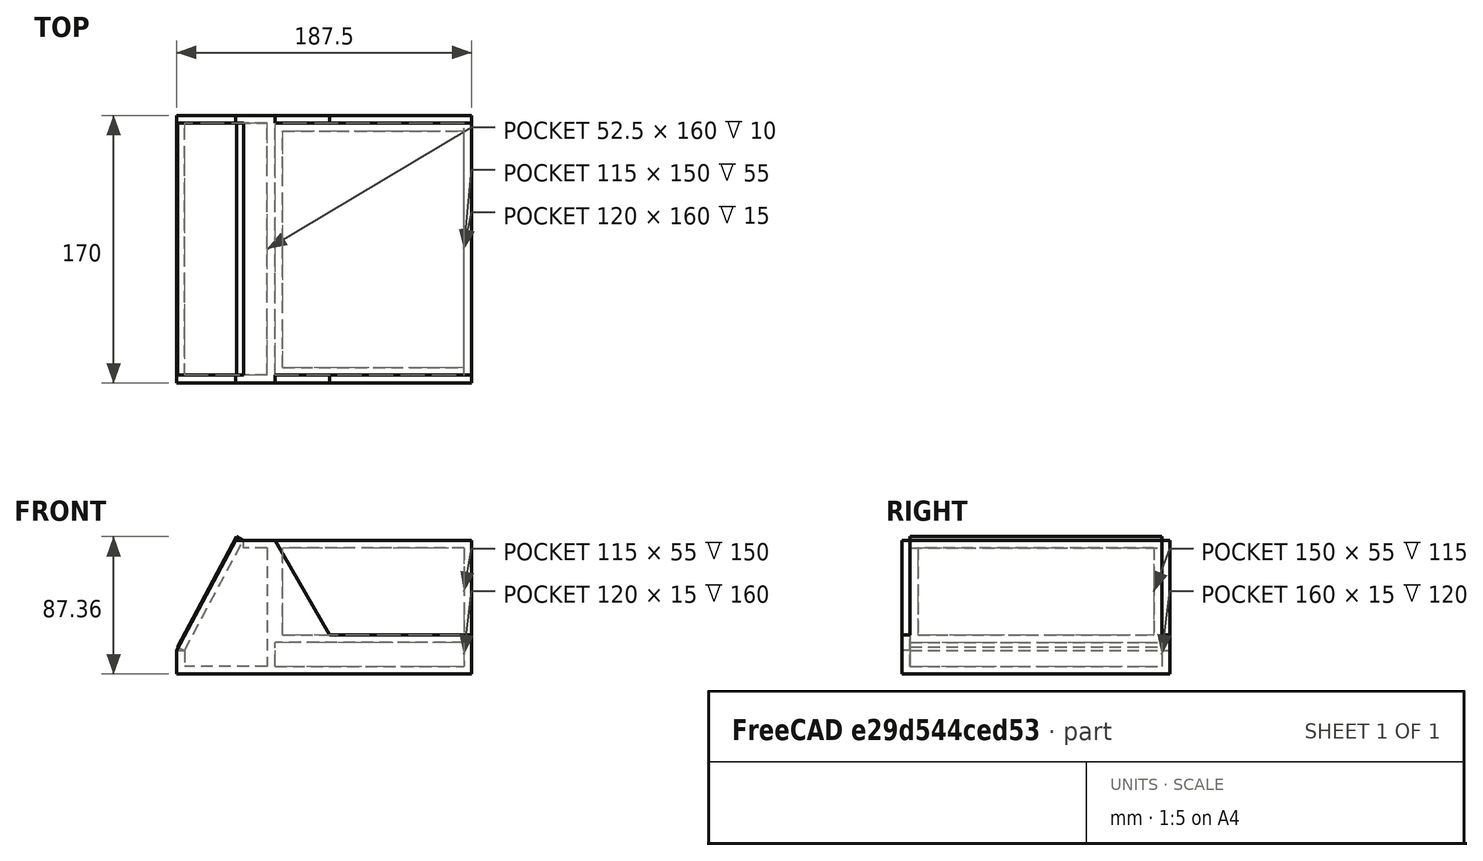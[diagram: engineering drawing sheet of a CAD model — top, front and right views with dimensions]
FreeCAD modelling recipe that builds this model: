
FCSTD DOCUMENT  (FreeCAD 0.17R13522 (Git))
Label: sheet model_no cut
License: All rights reserved
LicenseURL: http://en.wikipedia.org/wiki/All_rights_reserved
objects: Sketcher::SketchObject×12, PartDesign::Pad×12, PartDesign::Mirrored×2, PartDesign::Body×1
note: 39 computed .brp shape members not serialized (recipe doc carries the construction recipe); baked Part::Feature solids carry a one-line shape summary decoded from their .brp

FEATURE [Sketcher::SketchObject] Sketch
  MapMode = 5
  Support = -> [XY_Plane]
  sketch-geometry (4):
    g0: LineSegment StartX=-57.5 StartY=80 StartZ=0 EndX=120 EndY=80 EndZ=0
    g1: LineSegment StartX=120 StartY=80 StartZ=0 EndX=120 EndY=-80 EndZ=0
    g2: LineSegment StartX=120 StartY=-80 StartZ=0 EndX=-57.5 EndY=-80 EndZ=0
    g3: LineSegment StartX=-57.5 StartY=-80 StartZ=0 EndX=-57.5 EndY=80 EndZ=0
  constraints (12):
    c: Coincident(g0,g1)
    c: Coincident(g1,g2)
    c: Coincident(g2,g3)
    c: Coincident(g3,g0)
    c: Horizontal(g0)
    c: Horizontal(g2)
    c: Vertical(g1)
    c: Vertical(g3)
    c: DistanceY(g1,g1) = 160
    c: DistanceX(g0,g0) = 177.5
    c: DistanceY(g-1,g0) = 80
    c: DistanceX(g-1,g1) = 120
FEATURE [PartDesign::Pad] Pad
  Length = 5
  Length2 = 100
  Profile = -> Sketch
  Type = 0
FEATURE [Sketcher::SketchObject] Sketch001
  ExternalGeometry = -> [Pad]
  MapMode = 5
  Placement = pos=(0,-80,0) rot=(1,0,0;1.5708rad)
  Support = -> [Pad]
  sketch-geometry (4):
    g0: LineSegment StartX=-62.5 StartY=15 StartZ=0 EndX=-57.5 EndY=15 EndZ=0
    g1: LineSegment StartX=-57.5 StartY=15 StartZ=0 EndX=-57.5 EndY=0 EndZ=0
    g2: LineSegment StartX=-57.5 StartY=0 StartZ=0 EndX=-62.5 EndY=0 EndZ=0
    g3: LineSegment StartX=-62.5 StartY=0 StartZ=0 EndX=-62.5 EndY=15 EndZ=0
  constraints (12):
    c: Coincident(g0,g1)
    c: Coincident(g1,g2)
    c: Coincident(g2,g3)
    c: Coincident(g3,g0)
    c: Horizontal(g0)
    c: Horizontal(g2)
    c: Vertical(g1)
    c: Vertical(g3)
    c: Horizontal(g1,g-1)
    c: DistanceX(g2,g2) = 5
    c: Coincident(g1,g-3)
    c: DistanceY(g3,g3) = 15
FEATURE [PartDesign::Pad] Pad001
  BaseFeature = -> Pad
  Length = 160
  Length2 = 100
  Profile = -> Sketch001
  Reversed = true
  Type = 0
FEATURE [Sketcher::SketchObject] Sketch002
  ExternalGeometry = -> [Pad001]
  MapMode = 5
  Placement = pos=(0,-80,0) rot=(1,0,0;1.5708rad)
  Support = -> [Pad001]
  sketch-geometry (4):
    g0: LineSegment StartX=-5 StartY=5 StartZ=0 EndX=0 EndY=5 EndZ=0
    g1: LineSegment StartX=0 StartY=5 StartZ=0 EndX=0 EndY=80 EndZ=0
    g2: LineSegment StartX=0 StartY=80 StartZ=0 EndX=-5 EndY=80 EndZ=0
    g3: LineSegment StartX=-5 StartY=80 StartZ=0 EndX=-5 EndY=5 EndZ=0
  constraints (12):
    c: Coincident(g0,g1)
    c: Coincident(g1,g2)
    c: Coincident(g2,g3)
    c: Coincident(g3,g0)
    c: Horizontal(g0)
    c: Horizontal(g2)
    c: Vertical(g1)
    c: Vertical(g3)
    c: PointOnObject(g0,g-3)
    c: Vertical(g0,g-1)
    c: DistanceX(g0,g0) = 5
    c: DistanceY(g1,g1) = 75
FEATURE [PartDesign::Pad] Pad002
  BaseFeature = -> Pad001
  Length = 160
  Length2 = 100
  Profile = -> Sketch002
  Reversed = true
  Type = 0
FEATURE [Sketcher::SketchObject] Sketch003
  ExternalGeometry = -> [Pad002]
  MapMode = 5
  Placement = pos=(0,-80,0) rot=(1,0,0;1.5708rad)
  Support = -> [Pad002]
  sketch-geometry (4):
    g0: LineSegment StartX=-20 StartY=85 StartZ=0 EndX=0 EndY=85 EndZ=0
    g1: LineSegment StartX=0 StartY=85 StartZ=0 EndX=0 EndY=80 EndZ=0
    g2: LineSegment StartX=0 StartY=80 StartZ=0 EndX=-20 EndY=80 EndZ=0
    g3: LineSegment StartX=-20 StartY=80 StartZ=0 EndX=-20 EndY=85 EndZ=0
  constraints (11):
    c: Coincident(g0,g1)
    c: Coincident(g1,g2)
    c: Coincident(g2,g3)
    c: Coincident(g3,g0)
    c: Horizontal(g0)
    c: Horizontal(g2)
    c: Vertical(g1)
    c: Vertical(g3)
    c: Coincident(g1,g-3)
    c: DistanceY(g1,g1) = 5
    c: DistanceX(g0,g0) = 20
FEATURE [PartDesign::Pad] Pad003
  BaseFeature = -> Pad002
  Length = 160
  Length2 = 100
  Profile = -> Sketch003
  Reversed = true
  Type = 0
FEATURE [Sketcher::SketchObject] Sketch004
  ExternalGeometry = -> [Pad003]
  MapMode = 5
  Placement = pos=(0,-80,0) rot=(1,0,0;1.5708rad)
  Support = -> [Pad003]
  sketch-geometry (4):
    g0: LineSegment StartX=0 StartY=25 StartZ=0 EndX=120 EndY=25 EndZ=0
    g1: LineSegment StartX=120 StartY=25 StartZ=0 EndX=120 EndY=20 EndZ=0
    g2: LineSegment StartX=120 StartY=20 StartZ=0 EndX=0 EndY=20 EndZ=0
    g3: LineSegment StartX=0 StartY=20 StartZ=0 EndX=0 EndY=25 EndZ=0
  constraints (12):
    c: Coincident(g0,g1)
    c: Coincident(g1,g2)
    c: Coincident(g2,g3)
    c: Coincident(g3,g0)
    c: Horizontal(g0)
    c: Horizontal(g2)
    c: Vertical(g1)
    c: Vertical(g3)
    c: Vertical(g2,g-1)
    c: DistanceY(g1,g1) = 5
    c: Vertical(g1,g-3)
    c: DistanceY(g-3,g1) = 15
FEATURE [PartDesign::Pad] Pad004
  BaseFeature = -> Pad003
  Length = 160
  Length2 = 100
  Profile = -> Sketch004
  Reversed = true
  Type = 0
FEATURE [Sketcher::SketchObject] Sketch005
  ExternalGeometry = -> [Pad004]
  MapMode = 5
  Placement = pos=(120,0,0) rot=(0.57735,0.57735,0.57735;2.0944rad)
  Support = -> [Pad004]
  sketch-geometry (4):
    g0: LineSegment StartX=-80 StartY=25 StartZ=0 EndX=80 EndY=25 EndZ=0
    g1: LineSegment StartX=80 StartY=25 StartZ=0 EndX=80 EndY=0 EndZ=0
    g2: LineSegment StartX=80 StartY=0 StartZ=0 EndX=-80 EndY=0 EndZ=0
    g3: LineSegment StartX=-80 StartY=0 StartZ=0 EndX=-80 EndY=25 EndZ=0
  constraints (11):
    c: Coincident(g0,g1)
    c: Coincident(g1,g2)
    c: Coincident(g2,g3)
    c: Coincident(g3,g0)
    c: Horizontal(g0)
    c: Horizontal(g2)
    c: Vertical(g1)
    c: Vertical(g3)
    c: Coincident(g0,g-3)
    c: Coincident(g-4,g2)
    c: Coincident(g0,g-3)
FEATURE [PartDesign::Pad] Pad005
  BaseFeature = -> Pad004
  Length = 5
  Length2 = 100
  Profile = -> Sketch005
  Type = 0
FEATURE [Sketcher::SketchObject] Sketch006
  ExternalGeometry = -> [Pad005]
  MapMode = 5
  Placement = pos=(0,80,0) rot=(0,0.707107,0.707107;3.14159rad)
  Support = -> [Pad005]
  sketch-geometry (7):
    g0: LineSegment StartX=62.5 StartY=15 StartZ=0 EndX=62.5 EndY=0 EndZ=0
    g1: LineSegment StartX=62.5 StartY=0 StartZ=0 EndX=-125 EndY=0 EndZ=0
    g2: LineSegment StartX=-125 StartY=0 StartZ=0 EndX=-125 EndY=25 EndZ=0
    g3: LineSegment StartX=0 StartY=85 StartZ=0 EndX=-34.641 EndY=25 EndZ=0
    g4: LineSegment StartX=-125 StartY=25 StartZ=0 EndX=-34.641 EndY=25 EndZ=0
    g5: LineSegment StartX=0 StartY=85 StartZ=0 EndX=25 EndY=85 EndZ=0
    g6: LineSegment StartX=25 StartY=85 StartZ=0 EndX=62.5 EndY=15 EndZ=0
  constraints (16):
    c: Coincident(g2,g-3)
    c: Coincident(g2,g-3)
    c: Coincident(g2,g1)
    c: Coincident(g1,g-4)
    c: Coincident(g0,g1)
    c: Horizontal(g3,g2)
    c: Angle(g3,g-5) = 2.0944
    c: Coincident(g4,g3)
    c: Coincident(g4,g2)
    c: Coincident(g3,g-5)
    c: Coincident(g3,g5)
    c: Horizontal(g5)
    c: DistanceX(g-5,g5) = 5
    c: Coincident(g6,g0)
    c: Coincident(g0,g-4)
    c: Coincident(g5,g6)
FEATURE [PartDesign::Pad] Pad006
  BaseFeature = -> Pad005
  Length = 5
  Length2 = 100
  Profile = -> Sketch006
  Type = 0
FEATURE [Sketcher::SketchObject] Sketch007
  ExternalGeometry = -> [Pad006]
  MapMode = 5
  Placement = pos=(0,-80,0) rot=(1,0,0;1.5708rad)
  Support = -> [Pad006]
  sketch-geometry (4):
    g0: LineSegment StartX=-57.5 StartY=15 StartZ=0 EndX=-20 EndY=85 EndZ=0
    g1: LineSegment StartX=-24.4074 StartY=87.3611 StartZ=0 EndX=-20 EndY=85 EndZ=0
    g2: LineSegment StartX=-61.9074 StartY=17.3611 StartZ=0 EndX=-57.5 EndY=15 EndZ=0
    g3: LineSegment StartX=-24.4074 StartY=87.3611 StartZ=0 EndX=-61.9074 EndY=17.3611 EndZ=0
  constraints (10):
    c: Coincident(g0,g-4)
    c: Coincident(g0,g-3)
    c: Coincident(g1,g0)
    c: Coincident(g2,g0)
    c: Distance(g1) = 5
    c: Angle(g1,g0) = 1.5708
    c: Parallel(g2,g1)
    c: Distance(g2) = 5
    c: Coincident(g3,g1)
    c: Coincident(g2,g3)
FEATURE [PartDesign::Pad] Pad007
  BaseFeature = -> Pad006
  Length = 160
  Length2 = 100
  Profile = -> Sketch007
  Reversed = true
  Type = 0
FEATURE [PartDesign::Mirrored] Mirrored
  BaseFeature = -> Pad007
  MirrorPlane = -> XZ_Plane
  Originals = -> [Pad006]
FEATURE [Sketcher::SketchObject] Sketch008
  ExternalGeometry = -> [Mirrored]
  MapMode = 5
  Placement = pos=(0,-80,0) rot=(0,0.707107,0.707107;3.14159rad)
  Support = -> [Mirrored]
  sketch-geometry (4):
    g0: LineSegment StartX=-125 StartY=85 StartZ=0 EndX=0 EndY=85 EndZ=0
    g1: LineSegment StartX=0 StartY=85 StartZ=0 EndX=0 EndY=25 EndZ=0
    g2: LineSegment StartX=0 StartY=25 StartZ=0 EndX=-125 EndY=25 EndZ=0
    g3: LineSegment StartX=-125 StartY=25 StartZ=0 EndX=-125 EndY=85 EndZ=0
  constraints (11):
    c: Coincident(g0,g1)
    c: Coincident(g1,g2)
    c: Coincident(g2,g3)
    c: Coincident(g3,g0)
    c: Horizontal(g0)
    c: Horizontal(g2)
    c: Vertical(g1)
    c: Vertical(g3)
    c: Coincident(g1,g-3)
    c: Coincident(g0,g-4)
    c: Coincident(g-5,g2)
FEATURE [PartDesign::Pad] Pad008
  BaseFeature = -> Mirrored
  Length = 5
  Length2 = 100
  Profile = -> Sketch008
  Type = 0
FEATURE [Sketcher::SketchObject] Sketch009
  ExternalGeometry = -> [Pad008]
  MapMode = 5
  Placement = pos=(0,-75,0) rot=(0,0.707107,0.707107;3.14159rad)
  Support = -> [Pad008]
  sketch-geometry (4):
    g0: LineSegment StartX=-125 StartY=85 StartZ=0 EndX=-120 EndY=85 EndZ=0
    g1: LineSegment StartX=-120 StartY=85 StartZ=0 EndX=-120 EndY=25 EndZ=0
    g2: LineSegment StartX=-120 StartY=25 StartZ=0 EndX=-125 EndY=25 EndZ=0
    g3: LineSegment StartX=-125 StartY=25 StartZ=0 EndX=-125 EndY=85 EndZ=0
  constraints (11):
    c: Coincident(g0,g1)
    c: Coincident(g1,g2)
    c: Coincident(g2,g3)
    c: Coincident(g3,g0)
    c: Horizontal(g0)
    c: Horizontal(g2)
    c: Vertical(g1)
    c: Vertical(g3)
    c: DistanceX(g0,g0) = 5
    c: Coincident(g0,g-3)
    c: Coincident(g2,g-3)
FEATURE [PartDesign::Pad] Pad009
  BaseFeature = -> Pad008
  Length = 150
  Length2 = 100
  Profile = -> Sketch009
  Type = 0
FEATURE [Sketcher::SketchObject] Sketch010
  ExternalGeometry = -> [Pad009]
  MapMode = 5
  Placement = pos=(0,-75,0) rot=(0,0.707107,0.707107;3.14159rad)
  Support = -> [Pad009]
  sketch-geometry (4):
    g0: LineSegment StartX=-5 StartY=85 StartZ=0 EndX=0 EndY=85 EndZ=0
    g1: LineSegment StartX=0 StartY=85 StartZ=0 EndX=0 EndY=25 EndZ=0
    g2: LineSegment StartX=0 StartY=25 StartZ=0 EndX=-5 EndY=25 EndZ=0
    g3: LineSegment StartX=-5 StartY=25 StartZ=0 EndX=-5 EndY=85 EndZ=0
  constraints (11):
    c: Coincident(g0,g1)
    c: Coincident(g1,g2)
    c: Coincident(g2,g3)
    c: Coincident(g3,g0)
    c: Horizontal(g0)
    c: Horizontal(g2)
    c: Vertical(g1)
    c: Vertical(g3)
    c: Coincident(g1,g-4)
    c: Horizontal(g0,g-3)
    c: DistanceX(g0,g0) = 5
FEATURE [PartDesign::Pad] Pad010
  BaseFeature = -> Pad009
  Length = 150
  Length2 = 100
  Profile = -> Sketch010
  Type = 0
FEATURE [PartDesign::Mirrored] Mirrored001
  BaseFeature = -> Pad010
  MirrorPlane = -> XZ_Plane
  Originals = -> [Pad008]
FEATURE [Sketcher::SketchObject] Sketch011
  ExternalGeometry = -> [Mirrored001]
  MapMode = 5
  Placement = pos=(0,0,85) rot=(0,0,1;0rad)
  Support = -> [Mirrored001]
  sketch-geometry (4):
    g0: LineSegment StartX=5 StartY=75 StartZ=0 EndX=120 EndY=75 EndZ=0
    g1: LineSegment StartX=120 StartY=75 StartZ=0 EndX=120 EndY=-75 EndZ=0
    g2: LineSegment StartX=120 StartY=-75 StartZ=0 EndX=5 EndY=-75 EndZ=0
    g3: LineSegment StartX=5 StartY=-75 StartZ=0 EndX=5 EndY=75 EndZ=0
  constraints (10):
    c: Coincident(g0,g1)
    c: Coincident(g1,g2)
    c: Coincident(g2,g3)
    c: Coincident(g3,g0)
    c: Horizontal(g0)
    c: Horizontal(g2)
    c: Vertical(g1)
    c: Vertical(g3)
    c: Coincident(g1,g-4)
    c: Coincident(g0,g-3)
FEATURE [PartDesign::Pad] Pad011
  BaseFeature = -> Mirrored001
  Length = 5
  Length2 = 100
  Profile = -> Sketch011
  Reversed = true
  Type = 0
FEATURE [PartDesign::Body] Body
  Group = -> [Sketch,Pad,Sketch001,Pad001,Sketch002,Pad002,Sketch003,Pad003,Sketch004,Pad004,Sketch005,Pad005,Sketch006,Pad006,Sketch007,Pad007,Mirrored,Sketch008,Pad008,Sketch009,Pad009,Sketch010,Pad010,Mirrored001,Sketch011,Pad011]
  Origin = -> Origin
  Tip = -> Pad011
